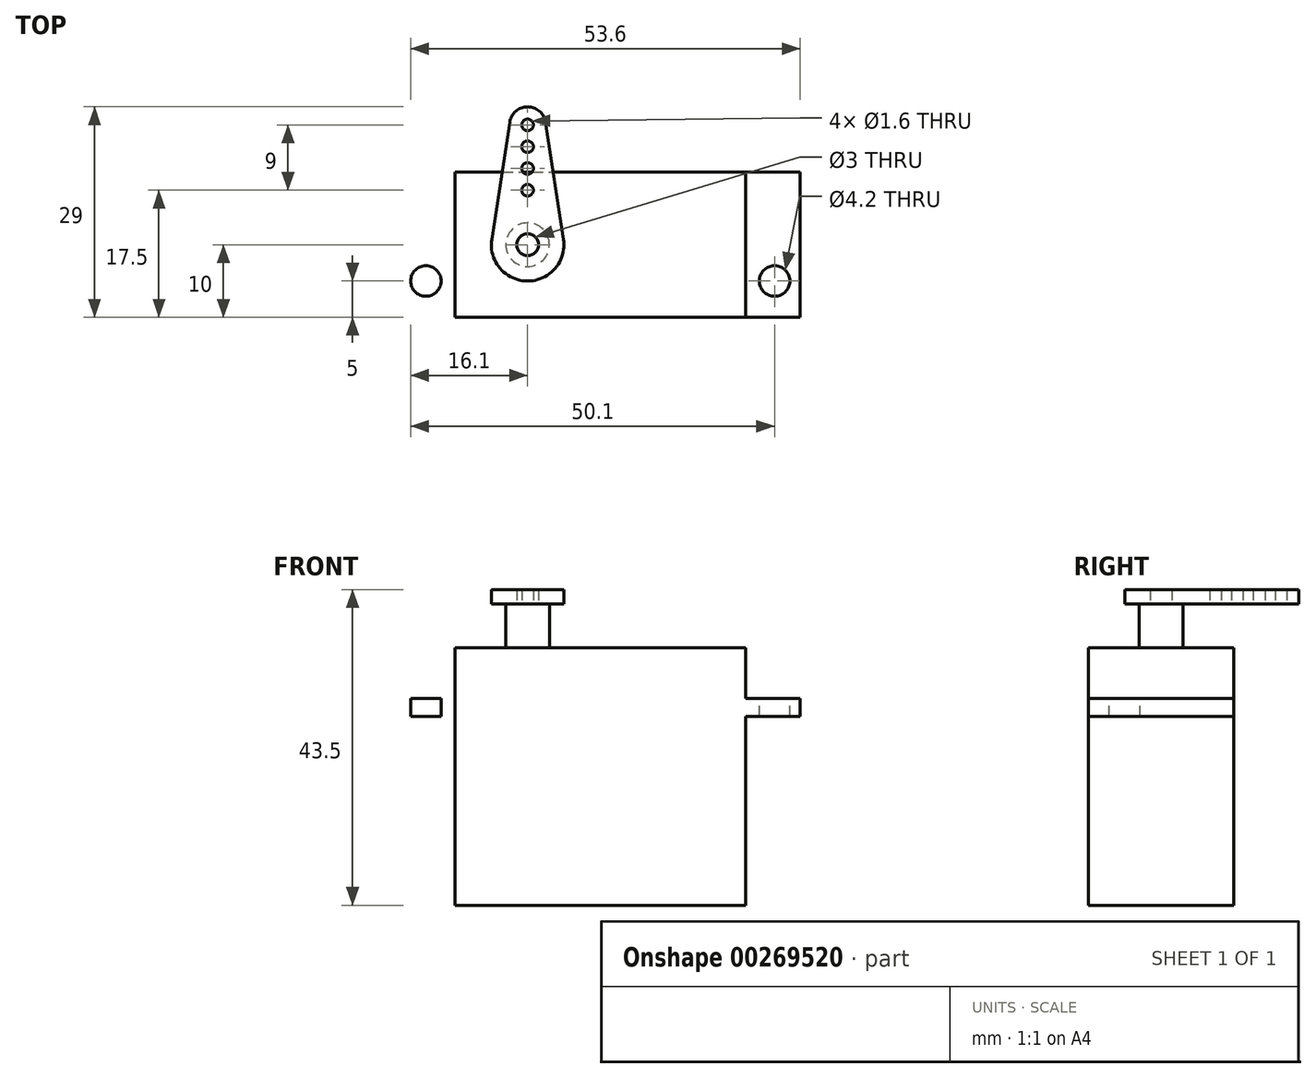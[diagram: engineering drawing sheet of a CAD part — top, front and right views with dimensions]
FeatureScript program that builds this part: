
annotation { "Feature Type Name" : "Feature", "Feature Type Description" : "" }
export const myFeature = defineFeature(function(context is Context, id is Id, definition is map)
    precondition{}
    {
        {
            var Q0;
            Q0=qCreatedBy(makeId("Front.planeOp"),FACE);
            var sketch = newSketch(context, id + "F0", { "sketchPlane" : qUnion([Q0])});
            skLineSegment(sketch, "E0", {"start": v(0, 0) * mm, "end": v(-20, 0) * mm});
            skLineSegment(sketch, "E1", {"start": v(-20, 0) * mm, "end": v(-20, -7) * mm});
            skLineSegment(sketch, "E2", {"start": v(-20, -7) * mm, "end": v(-27.5, -7) * mm});
            skLineSegment(sketch, "E3", {"start": v(-27.5, -7) * mm, "end": v(-27.5, -9.5) * mm});
            skLineSegment(sketch, "E4", {"start": v(-27.5, -9.5) * mm, "end": v(-20, -9.5) * mm});
            skLineSegment(sketch, "E5", {"start": v(-20, -9.5) * mm, "end": v(-20, -35.5) * mm});
            skLineSegment(sketch, "E6", {"start": v(-20, -35.5) * mm, "end": v(0, -35.5) * mm});
            skLineSegment(sketch, "E7.MirrorCS", {"start": v(0, 0) * mm, "end": v(20, 0) * mm});
            skLineSegment(sketch, "E8.MirrorCS", {"start": v(20, 0) * mm, "end": v(20, -7) * mm});
            skLineSegment(sketch, "E9.MirrorCS", {"start": v(20, -7) * mm, "end": v(27.5, -7) * mm});
            skLineSegment(sketch, "E10.MirrorCS", {"start": v(27.5, -7) * mm, "end": v(27.5, -9.5) * mm});
            skLineSegment(sketch, "E11.MirrorCS", {"start": v(27.5, -9.5) * mm, "end": v(20, -9.5) * mm});
            skLineSegment(sketch, "E12.MirrorCS", {"start": v(20, -9.5) * mm, "end": v(20, -35.5) * mm});
            skLineSegment(sketch, "E13.MirrorCS", {"start": v(20, -35.5) * mm, "end": v(0, -35.5) * mm});
            skSolve(sketch);
        }
        {
            var Q0;
            Q0=makeQuery(id+"F0.imprint","IMPRINT",FACE,{"disambiguationData":[TD([[makeQuery(id+"F0.imprint","IMPRINT",EDGE,{"derivedFrom":sQuery(id+"F0.wireOp",EDGE,"E0")}),1.0]])]});
            extrude(context, id + "F1", {"entities" : qUnion([Q0]), "endBound" : BoundingType.SYMMETRIC, "depth" : 20 * mm});
        }
        {
            var Q0;
            Q0=makeQuery(id+"F1.opExtrude","SWEPT_FACE",FACE,{"disambiguationData":[OSD([sQuery(id+"F0.wireOp",EDGE,"E0"),sQuery(id+"F0.wireOp",EDGE,"E7.MirrorCS")])]});
            var sketch = newSketch(context, id + "F2", { "sketchPlane" : qUnion([Q0])});
            skCircle(sketch, "E14", {"center": v(-10, 0) * mm, "radius": 3 * mm});
            skSolve(sketch);
        }
        {
            var Q0;
            Q0=makeQuery(id+"F2.imprint","IMPRINT",FACE,{"disambiguationData":[TD([[makeQuery(id+"F2.imprint","IMPRINT",EDGE,{"derivedFrom":sQuery(id+"F2.wireOp",EDGE,"E14")}),1.0]])]});
            extrude(context, id + "F3", {"entities" : qUnion([Q0]), "operationType" : NewBodyOperationType.ADD, "depth" : 6 * mm});
        }
        {
            var Q0;
            Q0=makeQuery(id+"F1.opExtrude","SWEPT_FACE",FACE,{"disambiguationData":[OSD([sQuery(id+"F0.wireOp",EDGE,"E2")])]});
            var sketch = newSketch(context, id + "F4", { "sketchPlane" : qUnion([Q0])});
            skCircle(sketch, "E15", {"center": v(-24, 5) * mm, "radius": 2.1 * mm});
            skCircle(sketch, "E16.MirrorC", {"center": v(-24, -5) * mm, "radius": 2.1 * mm});
            skCircle(sketch, "E17.MirrorC", {"center": v(24, 5) * mm, "radius": 2.1 * mm});
            skCircle(sketch, "E18.MirrorC", {"center": v(24, -5) * mm, "radius": 2.1 * mm});
            skSolve(sketch);
        }
        {
            var Q0;
            Q0=makeQuery(id+"F4.imprint","IMPRINT",FACE,{"disambiguationData":[TD([[makeQuery(id+"F4.imprint","IMPRINT",EDGE,{"derivedFrom":sQuery(id+"F4.wireOp",EDGE,"E15")}),1.0]])]});
            var Q1;
            Q1=makeQuery(id+"F4.imprint","IMPRINT",FACE,{"disambiguationData":[TD([[makeQuery(id+"F4.imprint","IMPRINT",EDGE,{"derivedFrom":sQuery(id+"F4.wireOp",EDGE,"E16.MirrorC")}),-1.0]])]});
            var Q2;
            Q2=makeQuery(id+"F4.imprint","IMPRINT",FACE,{"disambiguationData":[TD([[makeQuery(id+"F4.imprint","IMPRINT",EDGE,{"derivedFrom":sQuery(id+"F4.wireOp",EDGE,"E17.MirrorC")}),-1.0]])]});
            var Q3;
            Q3=makeQuery(id+"F4.imprint","IMPRINT",FACE,{"disambiguationData":[TD([[makeQuery(id+"F4.imprint","IMPRINT",EDGE,{"derivedFrom":sQuery(id+"F4.wireOp",EDGE,"E18.MirrorC")}),1.0]])]});
            extrude(context, id + "F5", {"entities" : qUnion([Q0, Q1, Q2, Q3]), "operationType" : NewBodyOperationType.REMOVE, "endBound" : BoundingType.THROUGH_ALL, "oppositeDirection" : true, "depth" : 25 * mm});
        }
        {
            var Q0;
            Q0=makeQuery(id+"F3.opExtrude","CAP_FACE",FACE,{"disambiguationData":[OSD([sQuery(id+"F2.wireOp",EDGE,"E14")])],"isStart":false});
            var sketch = newSketch(context, id + "F6", { "sketchPlane" : qUnion([Q0])});
            skCircle(sketch, "E19.0", {"center": v(-10, 0) * mm, "radius": 3 * mm});
            skCircle(sketch, "E20", {"center": v(-10, 0) * mm, "radius": 1.5 * mm});
            skLineSegment(sketch, "E21", {"start": v(-10, 0) * mm, "end": v(-10, 16.5) * mm, "construction": true});
            skCircle(sketch, "E22", {"center": v(-10, 16.5) * mm, "radius": 0.8 * mm});
            skCircle(sketch, "E23", {"center": v(-10, 13.5) * mm, "radius": 0.8 * mm});
            skCircle(sketch, "E24", {"center": v(-10, 10.5) * mm, "radius": 0.8 * mm});
            skCircle(sketch, "E25", {"center": v(-10, 7.5) * mm, "radius": 0.8 * mm});
            skLineSegment(sketch, "E26", {"start": v(-14.94, 0.76) * mm, "end": v(-14.94, 0.76) * mm});
            skLineSegment(sketch, "E27", {"start": v(-7.53, 16.88) * mm, "end": v(-5.06, 0.76) * mm});
            skArc(sketch, "E28", {"start": v(-12.47, 16.88) * mm, "mid": v(-10, 14) * mm, "end": v(-7.53, 16.88) * mm, "construction": true});
            skArc(sketch, "E29", {"start": v(-7.53, 16.88) * mm, "mid": v(-10, 19) * mm, "end": v(-12.47, 16.88) * mm});
            skLineSegment(sketch, "E30", {"start": v(-14.94, 0.76) * mm, "end": v(-12.47, 16.88) * mm});
            skLineSegment(sketch, "E31", {"start": v(-5.06, 0.76) * mm, "end": v(-5.06, 0.76) * mm});
            skArc(sketch, "E32", {"start": v(-14.94, 0.76) * mm, "mid": v(-10, -5) * mm, "end": v(-5.06, 0.76) * mm});
            skArc(sketch, "E33", {"start": v(-5.06, 0.76) * mm, "mid": v(-10, 5) * mm, "end": v(-14.94, 0.76) * mm, "construction": true});
            skSolve(sketch);
        }
        {
            var Q0;
            Q0=makeQuery(id+"F6.imprint","IMPRINT",FACE,{"disambiguationData":[TD([[makeQuery(id+"F6.imprint","IMPRINT",EDGE,{"derivedFrom":sQuery(id+"F6.wireOp",EDGE,"E19.0")}),-1.0]])]});
            var Q1;
            Q1=makeQuery(id+"F6.imprint","IMPRINT",FACE,{"disambiguationData":[TD([[makeQuery(id+"F6.imprint","IMPRINT",EDGE,{"derivedFrom":sQuery(id+"F6.wireOp",EDGE,"E19.0")}),1.0]])]});
            extrude(context, id + "F7", {"entities" : qUnion([Q0, Q1]), "depth" : 2 * mm});
        }
    });
